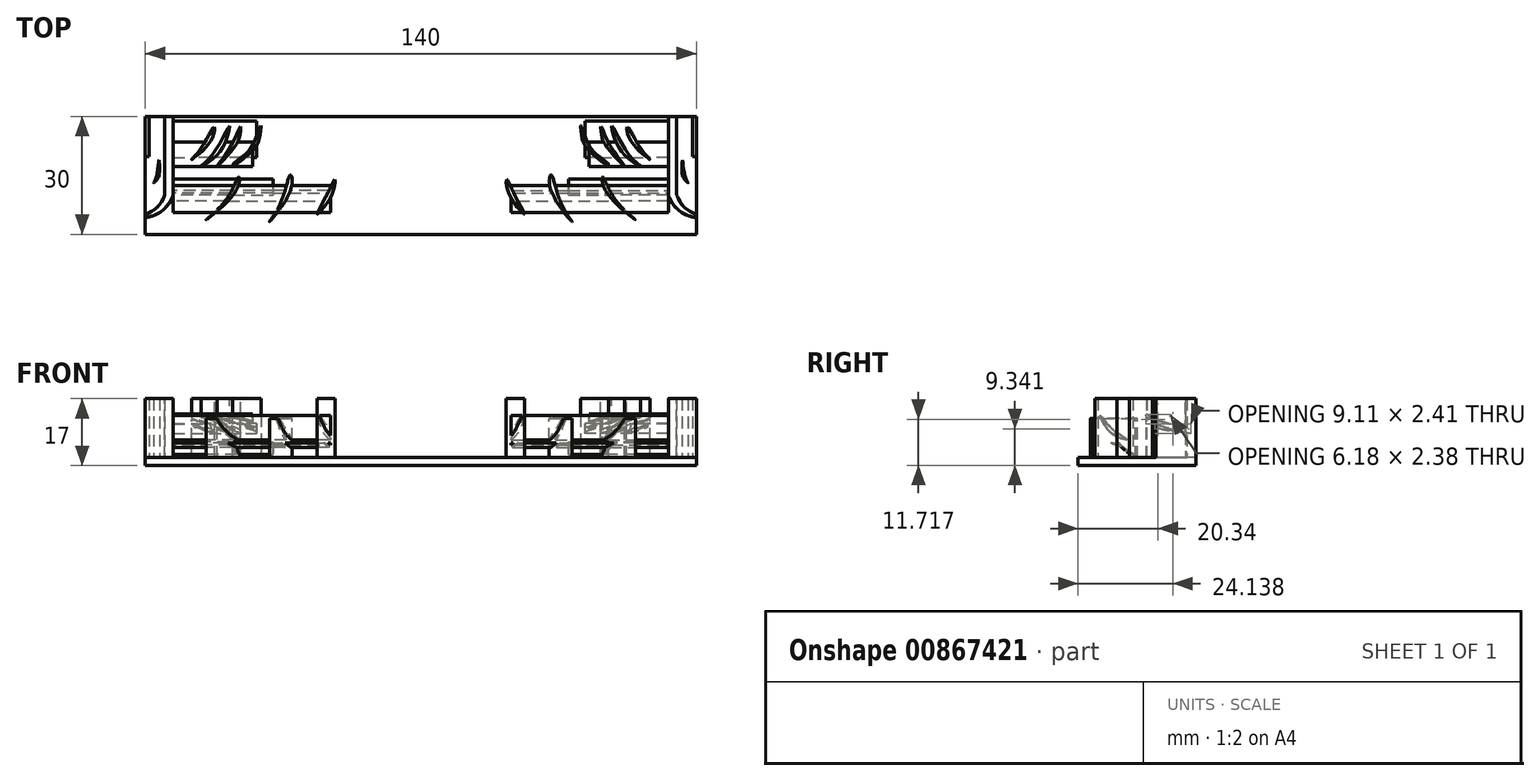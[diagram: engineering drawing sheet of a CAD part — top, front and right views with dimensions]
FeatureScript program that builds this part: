
annotation { "Feature Type Name" : "Feature", "Feature Type Description" : "" }
export const myFeature = defineFeature(function(context is Context, id is Id, definition is map)
    precondition{}
    {
        {
            var Q0;
            Q0=qCreatedBy(makeId("Top.planeOp"),FACE);
            var sketch = newSketch(context, id + "F0", { "sketchPlane" : qUnion([Q0])});
            skLineSegment(sketch, "E0.bottom", {"start": v(-44.94, 30) * mm, "end": v(25.06, 30) * mm});
            skLineSegment(sketch, "E0.top", {"start": v(-44.94, 0) * mm, "end": v(25.06, 0) * mm});
            skLineSegment(sketch, "E0.left", {"start": v(-44.94, 30) * mm, "end": v(-44.94, 0) * mm});
            skLineSegment(sketch, "E0.right", {"start": v(25.06, 30) * mm, "end": v(25.06, 0) * mm});
            skSolve(sketch);
        }
        {
            var Q0;
            Q0=makeQuery(id+"F0.imprint","IMPRINT",FACE,{"disambiguationData":[TD([[makeQuery(id+"F0.imprint","IMPRINT",EDGE,{"derivedFrom":sQuery(id+"F0.wireOp",EDGE,"E0.bottom")}),-1.0]])]});
            extrude(context, id + "F1", {"entities" : qUnion([Q0]), "depth" : 2 * mm, "offsetDistance" : 25.4 * mm});
        }
        {
            var Q0;
            Q0=makeQuery(id+"F1.opExtrude","CAP_FACE",FACE,{"disambiguationData":[OSD([sQuery(id+"F0.wireOp",EDGE,"E0.bottom"),sQuery(id+"F0.wireOp",EDGE,"E0.top"),sQuery(id+"F0.wireOp",EDGE,"E0.left"),sQuery(id+"F0.wireOp",EDGE,"E0.right")])],"isStart":false});
            var sketch = newSketch(context, id + "F2", { "sketchPlane" : qUnion([Q0])});
            skLineSegment(sketch, "E1", {"start": v(-44.94, 26.83) * mm, "end": v(-39.95, 26.83) * mm});
            skLineSegment(sketch, "E2.bottom", {"start": v(-39.95, 30) * mm, "end": v(-37.86, 30) * mm});
            skLineSegment(sketch, "E2.top", {"start": v(-39.95, 9.95) * mm, "end": v(-37.86, 9.95) * mm});
            skLineSegment(sketch, "E2.left", {"start": v(-39.95, 30) * mm, "end": v(-39.95, 9.95) * mm});
            skLineSegment(sketch, "E2.right", {"start": v(-37.86, 30) * mm, "end": v(-37.86, 9.95) * mm});
            skSolve(sketch);
        }
        {
            var Q0;
            {var subQ1=sQuery(id+"F2.wireOp",EDGE,"E1");Q0=makeQuery(id+"F2.imprint","IMPRINT",FACE,{"disambiguationData":[TD([[makeQuery(id+"F2.imprint","IMPRINT",EDGE,{"derivedFrom":subQ1}),-1.0]])]});}
            var sketch = newSketch(context, id + "F3", { "sketchPlane" : qUnion([Q0])});
            skFitSpline(sketch, "E3", {"points": [v(-39.95, 9.95) * mm, v(-41.75, 7.03) * mm, v(-44.92, 4.77) * mm, v(-44.86, 4.35) * mm, v(-44.86, 4.32) * mm, v(-40.84, 5.83) * mm, v(-37.87, 9.95) * mm, v(-37.96, 10) * mm, v(-38.13, 10) * mm, v(-39.72, 10) * mm, v(-39.95, 9.95) * mm]});
            skSolve(sketch);
        }
        {
            var Q0;
            {var subQ3=sQuery(id+"F2.wireOp",EDGE,"E2.bottom");Q0=makeQuery(id+"F2.imprint","IMPRINT",FACE,{"disambiguationData":[TD([[makeQuery(id+"F2.imprint","IMPRINT",EDGE,{"derivedFrom":subQ3}),-1.0]])]});}
            extrude(context, id + "F4", {"entities" : qUnion([Q0]), "operationType" : NewBodyOperationType.ADD, "depth" : 15 * mm, "offsetDistance" : 25.4 * mm});
        }
        {
            var Q0;
            {var subQ0=sQuery(id+"F3.wireOp",EDGE,"E3");var subQ2=sQuery(id+"F2.wireOp",EDGE,"E2.top");var subQ3=makeQuery(id+"F2.imprint","IMPRINT",EDGE,{"derivedFrom":subQ2});var subQ5=makeQuery(id+"F3.imprint","INTERSECT",VERTEX,{"derivedFrom":[subQ3,subQ0]});Q0=makeQuery(id+"F3.imprint","IMPRINT",FACE,{"disambiguationData":[TD([[makeQuery(id+"F3.imprint","IMPRINT",EDGE,{"disambiguationData":[TD([[subQ5,1.0]])],"derivedFrom":subQ0}),1.0]])]});}
            extrude(context, id + "F5", {"entities" : qUnion([Q0]), "operationType" : NewBodyOperationType.ADD, "depth" : 15 * mm, "offsetDistance" : 25.4 * mm});
        }
        {
            var Q0;
            Q0=makeQuery(id+"F1.opExtrude","CAP_FACE",FACE,{"disambiguationData":[OSD([sQuery(id+"F0.wireOp",EDGE,"E0.bottom"),sQuery(id+"F0.wireOp",EDGE,"E0.top"),sQuery(id+"F0.wireOp",EDGE,"E0.left"),sQuery(id+"F0.wireOp",EDGE,"E0.right")])],"isStart":false});
            var sketch = newSketch(context, id + "F6", { "sketchPlane" : qUnion([Q0])});
            skFitSpline(sketch, "E4", {"points": [v(-20.71, 27.44) * mm, v(-20.88, 25.23) * mm, v(-22.64, 21.6) * mm, v(-26.72, 17.35) * mm, v(-23.03, 22.59) * mm, v(-20.71, 27.44) * mm]});
            skSolve(sketch);
        }
        {
            var Q0;
            Q0=makeQuery(id+"F6.imprint","IMPRINT",FACE,{"disambiguationData":[TD([[makeQuery(id+"F6.imprint","IMPRINT",EDGE,{"derivedFrom":sQuery(id+"F6.wireOp",EDGE,"E4")}),1.0]])]});
            var sketch = newSketch(context, id + "F7", { "sketchPlane" : qUnion([Q0])});
            skFitSpline(sketch, "E5", {"points": [v(-23.54, 27.48) * mm, v(-23.81, 25.58) * mm, v(-27.29, 19.56) * mm, v(-30.77, 17.43) * mm, v(-28.27, 19.72) * mm, v(-23.54, 27.48) * mm]});
            skSolve(sketch);
        }
        {
            var Q0;
            Q0=makeQuery(id+"F6.imprint","IMPRINT",FACE,{"disambiguationData":[TD([[makeQuery(id+"F6.imprint","IMPRINT",EDGE,{"derivedFrom":sQuery(id+"F6.wireOp",EDGE,"E4")}),1.0]])]});
            var sketch = newSketch(context, id + "F8", { "sketchPlane" : qUnion([Q0])});
            skFitSpline(sketch, "E6", {"points": [v(-27.4, 27.3) * mm, v(-27.62, 25.2) * mm, v(-31.14, 20.53) * mm, v(-33.19, 19) * mm, v(-30.69, 22) * mm, v(-27.4, 27.3) * mm]});
            skSolve(sketch);
        }
        {
            var Q0;
            Q0=makeQuery(id+"F6.imprint","IMPRINT",FACE,{"disambiguationData":[TD([[makeQuery(id+"F6.imprint","IMPRINT",EDGE,{"derivedFrom":sQuery(id+"F6.wireOp",EDGE,"E4")}),1.0]])]});
            var sketch = newSketch(context, id + "F9", { "sketchPlane" : qUnion([Q0])});
            skFitSpline(sketch, "E7", {"points": [v(-15.57, 27.64) * mm, v(-15.74, 25.36) * mm, v(-17.56, 21.44) * mm, v(-22.68, 17.52) * mm, v(-22, 18.43) * mm, v(-18.01, 22.07) * mm, v(-15.57, 27.64) * mm]});
            skSolve(sketch);
        }
        {
            var Q0;
            Q0=makeQuery(id+"F6.imprint","IMPRINT",FACE,{"disambiguationData":[TD([[makeQuery(id+"F6.imprint","IMPRINT",EDGE,{"derivedFrom":sQuery(id+"F6.wireOp",EDGE,"E4")}),-1.0]])]});
            extrude(context, id + "F10", {"entities" : qUnion([Q0]), "operationType" : NewBodyOperationType.ADD, "depth" : 15 * mm, "offsetDistance" : 25.4 * mm});
        }
        {
            var Q0;
            Q0=makeQuery(id+"F7.imprint","IMPRINT",FACE,{"disambiguationData":[TD([[makeQuery(id+"F7.imprint","IMPRINT",EDGE,{"derivedFrom":sQuery(id+"F7.wireOp",EDGE,"E5")}),-1.0]])]});
            extrude(context, id + "F11", {"entities" : qUnion([Q0]), "operationType" : NewBodyOperationType.ADD, "depth" : 15 * mm, "offsetDistance" : 25.4 * mm});
        }
        {
            var Q0;
            Q0=makeQuery(id+"F8.imprint","IMPRINT",FACE,{"disambiguationData":[TD([[makeQuery(id+"F8.imprint","IMPRINT",EDGE,{"derivedFrom":sQuery(id+"F8.wireOp",EDGE,"E6")}),-1.0]])]});
            extrude(context, id + "F12", {"entities" : qUnion([Q0]), "operationType" : NewBodyOperationType.ADD, "depth" : 15 * mm, "offsetDistance" : 25.4 * mm});
        }
        {
            var Q0;
            Q0=makeQuery(id+"F9.imprint","IMPRINT",FACE,{"disambiguationData":[TD([[makeQuery(id+"F9.imprint","IMPRINT",EDGE,{"derivedFrom":sQuery(id+"F9.wireOp",EDGE,"E7")}),-1.0]])]});
            extrude(context, id + "F13", {"entities" : qUnion([Q0]), "operationType" : NewBodyOperationType.ADD, "depth" : 15 * mm, "offsetDistance" : 25.4 * mm});
        }
        {
            var Q0;
            Q0=makeQuery(id+"F4.opExtrude","SWEPT_FACE",FACE,{"disambiguationData":[OSD([sQuery(id+"F2.wireOp",EDGE,"E2.right")])]});
            var sketch = newSketch(context, id + "F14", { "sketchPlane" : qUnion([Q0])});
            skFitSpline(sketch, "E8", {"points": [v(28.7, 8.14) * mm, v(25.82, 8.47) * mm, v(19.6, 10.05) * mm, v(19.85, 10.62) * mm, v(20.51, 10.29) * mm, v(28.7, 8.14) * mm]});
            skSolve(sketch);
        }
        {
            var Q0;
            Q0=makeQuery(id+"F14.imprint","IMPRINT",FACE,{"disambiguationData":[TD([[makeQuery(id+"F14.imprint","IMPRINT",EDGE,{"derivedFrom":sQuery(id+"F14.wireOp",EDGE,"E8")}),1.0]])]});
            var sketch = newSketch(context, id + "F15", { "sketchPlane" : qUnion([Q0])});
            skFitSpline(sketch, "E9", {"points": [v(23.43, 10.53) * mm, v(19.9, 11.44) * mm, v(17.26, 12.49) * mm, v(17.4, 13.01) * mm, v(18.41, 12.4) * mm, v(23.43, 10.53) * mm]});
            skSolve(sketch);
        }
        {
            var Q0;
            Q0=makeQuery(id+"F14.imprint","IMPRINT",FACE,{"disambiguationData":[TD([[makeQuery(id+"F14.imprint","IMPRINT",EDGE,{"derivedFrom":sQuery(id+"F14.wireOp",EDGE,"E8")}),-1.0]])]});
            extrude(context, id + "F16", {"entities" : qUnion([Q0]), "operationType" : NewBodyOperationType.ADD, "depth" : 21.23 * mm, "offsetDistance" : 25.4 * mm});
        }
        {
            var Q0;
            Q0=makeQuery(id+"F15.imprint","IMPRINT",FACE,{"disambiguationData":[TD([[makeQuery(id+"F15.imprint","IMPRINT",EDGE,{"derivedFrom":sQuery(id+"F15.wireOp",EDGE,"E9")}),-1.0]])]});
            extrude(context, id + "F17", {"entities" : qUnion([Q0]), "operationType" : NewBodyOperationType.ADD, "depth" : 20.22 * mm, "offsetDistance" : 25.4 * mm});
        }
        {
            var Q0;
            Q0=makeQuery(id+"F4.opExtrude","SWEPT_FACE",FACE,{"disambiguationData":[OSD([sQuery(id+"F2.wireOp",EDGE,"E2.right")])]});
            var sketch = newSketch(context, id + "F18", { "sketchPlane" : qUnion([Q0])});
            skFitSpline(sketch, "E10", {"points": [v(14.05, 2.95) * mm, v(12.94, 3.11) * mm, v(9.95, 6.01) * mm, v(10.85, 5.26) * mm, v(12.94, 3.64) * mm, v(14.05, 2.95) * mm]});
            skSolve(sketch);
        }
        {
            var Q0;
            Q0=makeQuery(id+"F1.opExtrude","CAP_FACE",FACE,{"disambiguationData":[OSD([sQuery(id+"F0.wireOp",EDGE,"E0.bottom"),sQuery(id+"F0.wireOp",EDGE,"E0.top"),sQuery(id+"F0.wireOp",EDGE,"E0.left"),sQuery(id+"F0.wireOp",EDGE,"E0.right")])],"isStart":false});
            var sketch = newSketch(context, id + "F19", { "sketchPlane" : qUnion([Q0])});
            skLineSegment(sketch, "E11.bottom", {"start": v(-44.94, 30) * mm, "end": v(-43.97, 30) * mm});
            skLineSegment(sketch, "E11.top", {"start": v(-44.94, 19.78) * mm, "end": v(-43.97, 19.78) * mm});
            skLineSegment(sketch, "E11.left", {"start": v(-44.94, 30) * mm, "end": v(-44.94, 19.78) * mm});
            skLineSegment(sketch, "E11.right", {"start": v(-43.97, 30) * mm, "end": v(-43.97, 19.78) * mm});
            skSolve(sketch);
        }
        {
            var Q0;
            Q0=makeQuery(id+"F19.imprint","IMPRINT",FACE,{"disambiguationData":[TD([[makeQuery(id+"F19.imprint","IMPRINT",EDGE,{"derivedFrom":sQuery(id+"F19.wireOp",EDGE,"E11.bottom")}),-1.0]])]});
            extrude(context, id + "F20", {"entities" : qUnion([Q0]), "operationType" : NewBodyOperationType.ADD, "depth" : 15 * mm, "offsetDistance" : 25.4 * mm});
        }
        {
            var Q0;
            Q0=makeQuery(id+"F1.opExtrude","CAP_FACE",FACE,{"disambiguationData":[OSD([sQuery(id+"F0.wireOp",EDGE,"E0.bottom"),sQuery(id+"F0.wireOp",EDGE,"E0.top"),sQuery(id+"F0.wireOp",EDGE,"E0.left"),sQuery(id+"F0.wireOp",EDGE,"E0.right")])],"isStart":false});
            var sketch = newSketch(context, id + "F21", { "sketchPlane" : qUnion([Q0])});
            skFitSpline(sketch, "E12", {"points": [v(-41.45, 18.92) * mm, v(-41.32, 15.93) * mm, v(-41.94, 13.97) * mm, v(-42.84, 13.12) * mm, v(-42.18, 14.45) * mm, v(-41.45, 18.92) * mm]});
            skSolve(sketch);
        }
        {
            var Q0;
            Q0=makeQuery(id+"F21.imprint","IMPRINT",FACE,{"disambiguationData":[TD([[makeQuery(id+"F21.imprint","IMPRINT",EDGE,{"derivedFrom":sQuery(id+"F21.wireOp",EDGE,"E12")}),-1.0]])]});
            extrude(context, id + "F22", {"entities" : qUnion([Q0]), "operationType" : NewBodyOperationType.ADD, "depth" : 15 * mm, "offsetDistance" : 25.4 * mm});
        }
        {
            var Q0;
            Q0=makeQuery(id+"F18.imprint","IMPRINT",FACE,{"disambiguationData":[TD([[makeQuery(id+"F18.imprint","IMPRINT",EDGE,{"derivedFrom":sQuery(id+"F18.wireOp",EDGE,"E10")}),-1.0]])]});
            extrude(context, id + "F23", {"entities" : qUnion([Q0]), "operationType" : NewBodyOperationType.ADD, "depth" : 25.4 * mm, "offsetDistance" : 25.4 * mm});
        }
        {
            var Q0;
            Q0=makeQuery(id+"F4.opExtrude","SWEPT_FACE",FACE,{"disambiguationData":[OSD([sQuery(id+"F2.wireOp",EDGE,"E2.right")])]});
            var sketch = newSketch(context, id + "F24", { "sketchPlane" : qUnion([Q0])});
            skFitSpline(sketch, "E13", {"points": [v(13.52, 4.58) * mm, v(12.04, 4.51) * mm, v(10.44, 4.83) * mm, v(8.45, 5.73) * mm, v(10.57, 5.22) * mm, v(13.52, 4.58) * mm]});
            skSolve(sketch);
        }
        {
            var Q0;
            {var subQ0=sQuery(id+"F24.wireOp",EDGE,"E13");var subQ1=sQuery(id+"F2.wireOp",EDGE,"E2.top");var subQ2=makeQuery(id+"F5.boolean.opBoolean","MERGE",EDGE,{"derivedFrom":[makeQuery(id+"F4.opExtrude","SWEPT_EDGE",EDGE,{"disambiguationData":[OSD([subQ1,sQuery(id+"F2.wireOp",EDGE,"E2.right")])]}),makeQuery(id+"F5.opExtrude","SWEPT_EDGE",EDGE,{"disambiguationData":[OSD([subQ1,sQuery(id+"F3.wireOp",EDGE,"E3")])]})]});var subQ3=makeQuery(id+"F24.imprint","INTERSECT",VERTEX,{"disambiguationData":[OD(0.0)],"derivedFrom":[subQ2,subQ0]});Q0=makeQuery(id+"F24.imprint","IMPRINT",FACE,{"disambiguationData":[TD([[makeQuery(id+"F24.imprint","IMPRINT",EDGE,{"disambiguationData":[TD([[subQ3,-1.0]])],"derivedFrom":subQ0}),-1.0]])]});}
            var Q1;
            {var subQ0=sQuery(id+"F24.wireOp",EDGE,"E13");var subQ1=sQuery(id+"F2.wireOp",EDGE,"E2.top");var subQ2=makeQuery(id+"F5.boolean.opBoolean","MERGE",EDGE,{"derivedFrom":[makeQuery(id+"F4.opExtrude","SWEPT_EDGE",EDGE,{"disambiguationData":[OSD([subQ1,sQuery(id+"F2.wireOp",EDGE,"E2.right")])]}),makeQuery(id+"F5.opExtrude","SWEPT_EDGE",EDGE,{"disambiguationData":[OSD([subQ1,sQuery(id+"F3.wireOp",EDGE,"E3")])]})]});var subQ3=makeQuery(id+"F24.imprint","INTERSECT",VERTEX,{"disambiguationData":[OD(0.0)],"derivedFrom":[subQ2,subQ0]});Q1=makeQuery(id+"F24.imprint","IMPRINT",FACE,{"disambiguationData":[TD([[makeQuery(id+"F24.imprint","IMPRINT",EDGE,{"disambiguationData":[TD([[subQ3,1.0]])],"derivedFrom":subQ0}),-1.0]])]});}
            extrude(context, id + "F25", {"entities" : qUnion([Q0, Q1]), "operationType" : NewBodyOperationType.ADD, "depth" : 40 * mm, "offsetDistance" : 25.4 * mm});
        }
        {
            var Q0;
            Q0=makeQuery(id+"F4.opExtrude","SWEPT_FACE",FACE,{"disambiguationData":[OSD([sQuery(id+"F2.wireOp",EDGE,"E2.right")])]});
            var sketch = newSketch(context, id + "F26", { "sketchPlane" : qUnion([Q0])});
            skFitSpline(sketch, "E14", {"points": [v(12.46, 6.57) * mm, v(8.52, 8.23) * mm, v(5.59, 12.75) * mm, v(8.9, 9.12) * mm, v(12.46, 6.57) * mm]});
            skSolve(sketch);
        }
        {
            var Q0;
            {var subQ0=sQuery(id+"F26.wireOp",EDGE,"E14");var subQ1=sQuery(id+"F3.wireOp",EDGE,"E3");var subQ2=sQuery(id+"F2.wireOp",EDGE,"E2.top");var subQ3=sQuery(id+"F2.wireOp",EDGE,"E2.right");var subQ5=makeQuery(id+"F5.boolean.opBoolean","MERGE",EDGE,{"derivedFrom":[makeQuery(id+"F4.opExtrude","SWEPT_EDGE",EDGE,{"disambiguationData":[OSD([subQ2,subQ3])]}),makeQuery(id+"F5.opExtrude","SWEPT_EDGE",EDGE,{"disambiguationData":[OSD([subQ2,subQ1])]})]});var subQ8=makeQuery(id+"F25.boolean.opBoolean","SPLIT",EDGE,{"disambiguationData":[TD([makeQuery(id+"F5.opExtrude","CAP_FACE",FACE,{"disambiguationData":[OSD([subQ2,subQ1])],"isStart":false})])],"derivedFrom":subQ5});var subQ9=makeQuery(id+"F26.imprint","INTERSECT",VERTEX,{"disambiguationData":[OD(0.0)],"derivedFrom":[subQ8,subQ0]});Q0=makeQuery(id+"F26.imprint","IMPRINT",FACE,{"disambiguationData":[TD([[makeQuery(id+"F26.imprint","IMPRINT",EDGE,{"disambiguationData":[TD([[subQ9,1.0]])],"derivedFrom":subQ0}),-1.0]])]});}
            var Q1;
            {var subQ0=sQuery(id+"F26.wireOp",EDGE,"E14");var subQ1=sQuery(id+"F3.wireOp",EDGE,"E3");var subQ2=sQuery(id+"F2.wireOp",EDGE,"E2.top");var subQ3=sQuery(id+"F2.wireOp",EDGE,"E2.right");var subQ5=makeQuery(id+"F5.boolean.opBoolean","MERGE",EDGE,{"derivedFrom":[makeQuery(id+"F4.opExtrude","SWEPT_EDGE",EDGE,{"disambiguationData":[OSD([subQ2,subQ3])]}),makeQuery(id+"F5.opExtrude","SWEPT_EDGE",EDGE,{"disambiguationData":[OSD([subQ2,subQ1])]})]});var subQ8=makeQuery(id+"F25.boolean.opBoolean","SPLIT",EDGE,{"disambiguationData":[TD([makeQuery(id+"F5.opExtrude","CAP_FACE",FACE,{"disambiguationData":[OSD([subQ2,subQ1])],"isStart":false})])],"derivedFrom":subQ5});var subQ9=makeQuery(id+"F26.imprint","INTERSECT",VERTEX,{"disambiguationData":[OD(0.0)],"derivedFrom":[subQ8,subQ0]});Q1=makeQuery(id+"F26.imprint","IMPRINT",FACE,{"disambiguationData":[TD([[makeQuery(id+"F26.imprint","IMPRINT",EDGE,{"disambiguationData":[TD([[subQ9,-1.0]])],"derivedFrom":subQ0}),-1.0]])]});}
            extrude(context, id + "F27", {"entities" : qUnion([Q0, Q1]), "operationType" : NewBodyOperationType.ADD, "depth" : 40 * mm, "offsetDistance" : 25.4 * mm});
        }
        {
            var Q0;
            Q0=makeQuery(id+"F1.opExtrude","CAP_FACE",FACE,{"disambiguationData":[OSD([sQuery(id+"F0.wireOp",EDGE,"E0.bottom"),sQuery(id+"F0.wireOp",EDGE,"E0.top"),sQuery(id+"F0.wireOp",EDGE,"E0.left"),sQuery(id+"F0.wireOp",EDGE,"E0.right")])],"isStart":false});
            var sketch = newSketch(context, id + "F28", { "sketchPlane" : qUnion([Q0])});
            skFitSpline(sketch, "E15", {"points": [v(3.2, 13.92) * mm, v(2.6, 10.34) * mm, v(-1.25, 5.15) * mm, v(1.45, 10.47) * mm, v(3.2, 13.92) * mm]});
            skSolve(sketch);
        }
        {
            var Q0;
            Q0=makeQuery(id+"F28.imprint","IMPRINT",FACE,{"disambiguationData":[TD([[makeQuery(id+"F28.imprint","IMPRINT",EDGE,{"derivedFrom":sQuery(id+"F28.wireOp",EDGE,"E15")}),1.0]])]});
            var sketch = newSketch(context, id + "F29", { "sketchPlane" : qUnion([Q0])});
            skFitSpline(sketch, "E16", {"points": [v(-8.08, 15.12) * mm, v(-7.94, 11.46) * mm, v(-13.36, 3.23) * mm, v(-10.54, 8.08) * mm, v(-8.08, 15.12) * mm]});
            skSolve(sketch);
        }
        {
            var Q0;
            Q0=makeQuery(id+"F28.imprint","IMPRINT",FACE,{"disambiguationData":[TD([[makeQuery(id+"F28.imprint","IMPRINT",EDGE,{"derivedFrom":sQuery(id+"F28.wireOp",EDGE,"E15")}),1.0]])]});
            var sketch = newSketch(context, id + "F30", { "sketchPlane" : qUnion([Q0])});
            skFitSpline(sketch, "E17", {"points": [v(-21.16, 14.55) * mm, v(-22, 10.9) * mm, v(-29.46, 3.72) * mm, v(-24.4, 8.86) * mm, v(-21.16, 14.55) * mm]});
            skSolve(sketch);
        }
        {
            var Q0;
            Q0=makeQuery(id+"F28.imprint","IMPRINT",FACE,{"disambiguationData":[TD([[makeQuery(id+"F28.imprint","IMPRINT",EDGE,{"derivedFrom":sQuery(id+"F28.wireOp",EDGE,"E15")}),-1.0]])]});
            extrude(context, id + "F31", {"entities" : qUnion([Q0]), "operationType" : NewBodyOperationType.ADD, "depth" : 15 * mm, "offsetDistance" : 25.4 * mm});
        }
        {
            var Q0;
            Q0=makeQuery(id+"F29.imprint","IMPRINT",FACE,{"disambiguationData":[TD([[makeQuery(id+"F29.imprint","IMPRINT",EDGE,{"derivedFrom":sQuery(id+"F29.wireOp",EDGE,"E16")}),-1.0]])]});
            extrude(context, id + "F32", {"entities" : qUnion([Q0]), "operationType" : NewBodyOperationType.ADD, "depth" : 10 * mm, "offsetDistance" : 25.4 * mm});
        }
        {
            var Q0;
            Q0=makeQuery(id+"F30.imprint","IMPRINT",FACE,{"disambiguationData":[TD([[makeQuery(id+"F30.imprint","IMPRINT",EDGE,{"derivedFrom":sQuery(id+"F30.wireOp",EDGE,"E17")}),-1.0]])]});
            extrude(context, id + "F33", {"entities" : qUnion([Q0]), "operationType" : NewBodyOperationType.ADD, "depth" : 10 * mm, "offsetDistance" : 25.4 * mm});
        }
        {
            var Q0;
            Q0=makeQuery(id+"F1.opExtrude","SWEPT_BODY",BODY,{"disambiguationData":[OSD([sQuery(id+"F0.wireOp",EDGE,"E0.bottom"),sQuery(id+"F0.wireOp",EDGE,"E0.top"),sQuery(id+"F0.wireOp",EDGE,"E0.left"),sQuery(id+"F0.wireOp",EDGE,"E0.right")])]});
            var Q1;
            Q1=makeQuery(id+"F1.opExtrude","SWEPT_FACE",FACE,{"disambiguationData":[OSD([sQuery(id+"F0.wireOp",EDGE,"E0.right")])]});
            mirror(context, id + "F34", {"operationType" : NewBodyOperationType.ADD, "entities" : qUnion([Q0]), "mirrorPlane" : qUnion([Q1])});
        }
    });
